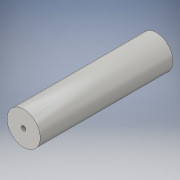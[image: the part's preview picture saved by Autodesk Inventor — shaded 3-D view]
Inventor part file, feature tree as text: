
AUTODESK INVENTOR PART (.ipt)
format: ipt  version: 2016 (Build 200138000, 138)  size: 113,664 bytes
history: native  units: in
note: dims shown in document units (in); Inventor stores cm internally (conversion verified against a paired STEP export)
features: sketch x3, extrude x2, hole x1, projected_geometry x1
ambient origin geometry x8: Origin, YZ Plane, XZ Plane, XY Plane, X Axis, Y Axis, Z Axis, Center Point
bodies: Solid1 (feature_tree)
feature tree (7):
  extrude  "Extrusion1"  Depth=3.0in TaperAngle=0.0deg
  extrude  "Extrusion2"  Depth=0.3in TaperAngle=0.0deg
  hole  "Hole1"  [1 undecoded]
  sketch  "Sketch1"  dims[d0=0.75in d1=3.0in d2=0.0in]
  sketch  "Sketch2"  dims[d3=0.1in d4=0.3in d5=0.0in]
  sketch  "Sketch3"  dims[d6=0.1in d7=0.75in d8=0.375in d9=0.25in d10=0.5635in d11=1.0in d12=0.8108in]
  projected_geometry  "Projected Loop1"
note: 1 required parameter value undecoded (feature->parameter linkage not recoverable at this tier; creation-order binding heuristic only, values carry confidence <= 0.55)
